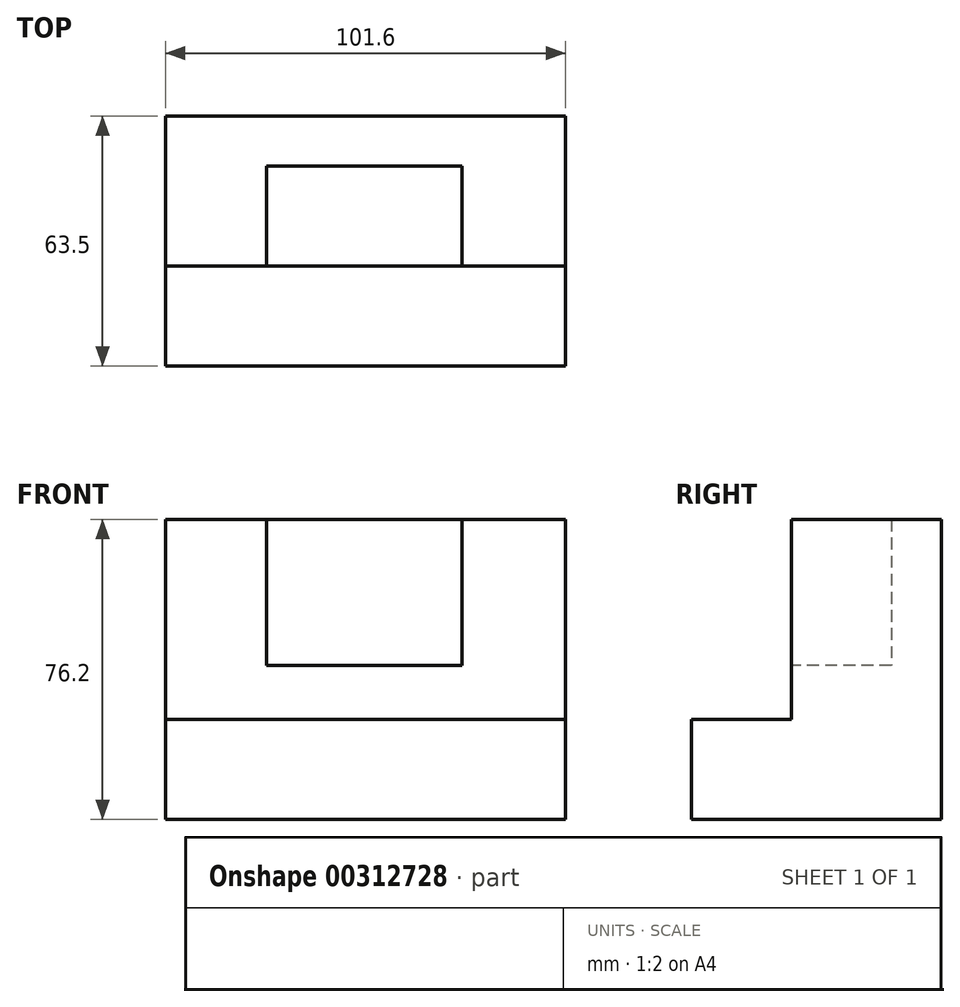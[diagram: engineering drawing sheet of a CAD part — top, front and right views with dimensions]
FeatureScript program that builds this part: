
annotation { "Feature Type Name" : "Feature", "Feature Type Description" : "" }
export const myFeature = defineFeature(function(context is Context, id is Id, definition is map)
    precondition{}
    {
        {
            var Q0;
            Q0=qCreatedBy(makeId("Right.planeOp"),FACE);
            var sketch = newSketch(context, id + "F0", { "sketchPlane" : qUnion([Q0])});
            skLineSegment(sketch, "E0", {"start": v(38.1, 28.86) * mm, "end": v(38.1, -47.34) * mm});
            skLineSegment(sketch, "E1", {"start": v(38.1, -47.34) * mm, "end": v(-25.4, -47.34) * mm});
            skLineSegment(sketch, "E2", {"start": v(-25.4, -47.34) * mm, "end": v(-25.4, -21.94) * mm});
            skLineSegment(sketch, "E3", {"start": v(-25.4, -21.94) * mm, "end": v(0, -21.94) * mm});
            skLineSegment(sketch, "E4", {"start": v(0, -21.94) * mm, "end": v(0, 28.86) * mm});
            skLineSegment(sketch, "E5", {"start": v(0, 28.86) * mm, "end": v(38.1, 28.86) * mm});
            skSolve(sketch);
        }
        {
            var Q0;
            Q0=makeQuery(id+"F0.imprint","IMPRINT",FACE,{"disambiguationData":[TD([[makeQuery(id+"F0.imprint","IMPRINT",EDGE,{"derivedFrom":sQuery(id+"F0.wireOp",EDGE,"E0")}),-1.0]])]});
            extrude(context, id + "F1", {"entities" : qUnion([Q0]), "depth" : 101.6 * mm});
        }
        {
            var Q0;
            Q0=makeQuery(id+"F1.opExtrude","SWEPT_FACE",FACE,{"disambiguationData":[OSD([sQuery(id+"F0.wireOp",EDGE,"E4")])]});
            var sketch = newSketch(context, id + "F2", { "sketchPlane" : qUnion([Q0])});
            skLineSegment(sketch, "E6", {"start": v(25.6, -8.23) * mm, "end": v(75.26, -8.23) * mm});
            skLineSegment(sketch, "E7", {"start": v(75.26, 28.86) * mm, "end": v(75.26, -8.23) * mm});
            skLineSegment(sketch, "E8", {"start": v(25.6, -8.23) * mm, "end": v(25.6, 28.86) * mm});
            skSolve(sketch);
        }
        {
            var Q0;
            Q0=makeQuery(id+"F2.imprint","IMPRINT",FACE,{"disambiguationData":[TD([[makeQuery(id+"F2.imprint","IMPRINT",EDGE,{"derivedFrom":sQuery(id+"F2.wireOp",EDGE,"E6")}),1.0]])]});
            extrude(context, id + "F3", {"entities" : qUnion([Q0]), "operationType" : NewBodyOperationType.REMOVE, "oppositeDirection" : true, "depth" : 25.4 * mm});
        }
    });
